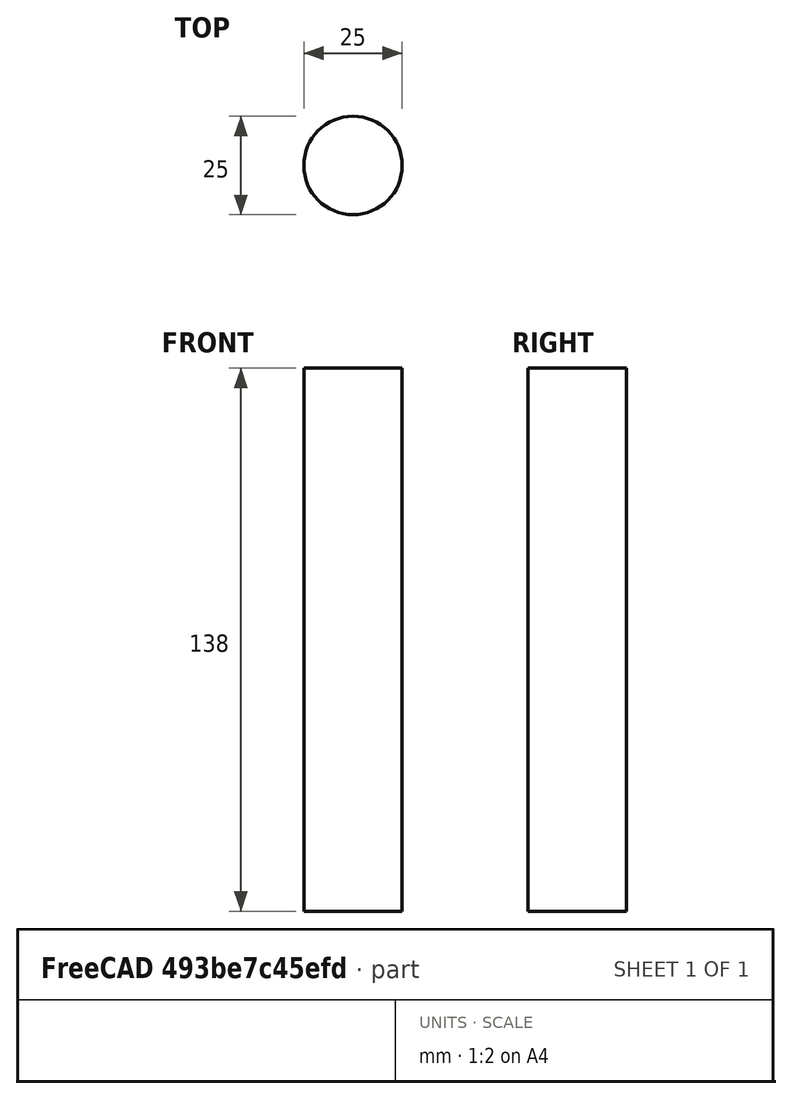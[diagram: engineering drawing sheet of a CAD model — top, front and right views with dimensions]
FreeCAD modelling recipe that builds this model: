
FCSTD DOCUMENT  (FreeCAD 0.16R)
Label: model2
License: All rights reserved
LicenseURL: http://en.wikipedia.org/wiki/All_rights_reserved
objects: Drawing::FeatureViewPart×2, Part::Cylinder×1, App::FeaturePython×1, App::DocumentObjectGroup×1, Drawing::FeaturePage×1
note: 1 computed .brp shape members not serialized (recipe doc carries the construction recipe); baked Part::Feature solids carry a one-line shape summary decoded from their .brp

FEATURE [Part::Cylinder] Cylinder
  Angle = 360
  Height = 138
  Radius = 12.5
FEATURE [App::FeaturePython] Dimension  # Draft dimension (typed FeaturePython)
  Dimline = (-12.5,0,0)
  Direction = (0,0,0)
  Distance = 25
  End = (-12.5,0,0)
  Normal = (0,0,1)
  Start = (12.5,0,0)
FEATURE [App::DocumentObjectGroup] Construction
  Group = -> [Dimension]
FEATURE [Drawing::FeatureViewPart] Ortho  label="Ortho_0_0"
  Direction = (1,0,0)
  HiddenWidth = 0.15
  LineWidth = 0.35
  Rotation = 180
  ShowHiddenLines = false
  ShowSmoothLines = false
  Source = -> Cylinder
  Tolerance = 0.05
  ViewResult = <g id="Ortho_0_0"\n   transform="rotate(180,248.967,81.5) translate(248.967,81.5) scale(1,1)"\n  >\n<g   stroke="rgb(0, 0, 0)"\n   stroke-width="0.35"\n   stroke-linecap="butt"\n   stroke-linejoin="miter"\n   fill="none"\n   transform="scale(1,-1)"\n  >\n<path id= "1" d=" M 0 -12.5 L 138 -12.5 " />\n<path id= "2" d=" M 0 12.5 L 138 12.5 " />\n</g>\n<g   stroke="rgb(0, 0, 0)"\n   stroke-width="0.35"\n   stroke-linecap="butt"\n   stroke-linejoin="miter"\n   fill="none"\n   transform="scale(1,-1)"\n  >\n<path d="M138,0 L138,-1.39956  L138,-2.78151  L138,-4.12849  L138,-5.42355  L138,-6.6504  L138,-7.79362  L138,-8.83883  L138,-9.77289  L138,-10.5841  L138,-11.2621  L138,-11.7985  L138,-12.1866  L138,-12.4214  L138,-12.5 " /><path d="M138,12.5 L138,12.4214  L138,12.1866  L138,11.7985  L138,11.2621  L138,10.5841  L138,9.77289  L138,8.83883  L138,7.79362  L138,6.6504  L138,5.42355  L138,4.12849  L138,2.78151  L138,1.39956  L138,3.06162e-15 " /><path d="M0,0 L0,-1.39956  L0,-2.78151  L0,-4.12849  L0,-5.42355  L0,-6.6504  L0,-7.79362  L0,-8.83883  L0,-9.77289  L0,-10.5841  L0,-11.2621  L0,-11.7985  L0,-12.1866  L0,-12.4214  L0,-12.5 " /><path d="M0,12.5 L0,12.4214  L0,12.1866  L0,11.7985  L0,11.2621  L0,10.5841  L0,9.77289  L0,8.83883  L0,7.79362  L0,6.6504  L0,5.42355  L0,4.12849  L0,2.78151  L0,1.39956  L0,3.06162e-15 " /></g>\n</g>
  Visible = true
  X = 248.967
  Y = 81.5
FEATURE [Drawing::FeatureViewPart] Ortho001  label="Ortho_-1_0"
  Direction = (0,0,1)
  HiddenWidth = 0.15
  LineWidth = 0.35
  Rotation = 0
  ShowHiddenLines = false
  ShowSmoothLines = false
  Source = -> Cylinder
  Tolerance = 0.05
  ViewResult = <g id="Ortho_-1_0"\n   transform="rotate(-6.36111e-15,60.4343,81.5) translate(60.4343,81.5) scale(1,1)"\n  >\n<g   stroke="rgb(0, 0, 0)"\n   stroke-width="0.35"\n   stroke-linecap="butt"\n   stroke-linejoin="miter"\n   fill="none"\n   transform="scale(1,-1)"\n  >\n<circle cx ="0" cy ="0" r ="12.5" /></g>\n</g>
  Visible = true
  X = 60.4343
  Y = 81.5
FEATURE [Drawing::FeaturePage] Page
  EditableTexts = Designed by Name | Date | Scale | Weight | Title | Subtitle | Drawing number | Sheet
  Group = -> [Ortho,Ortho001]
